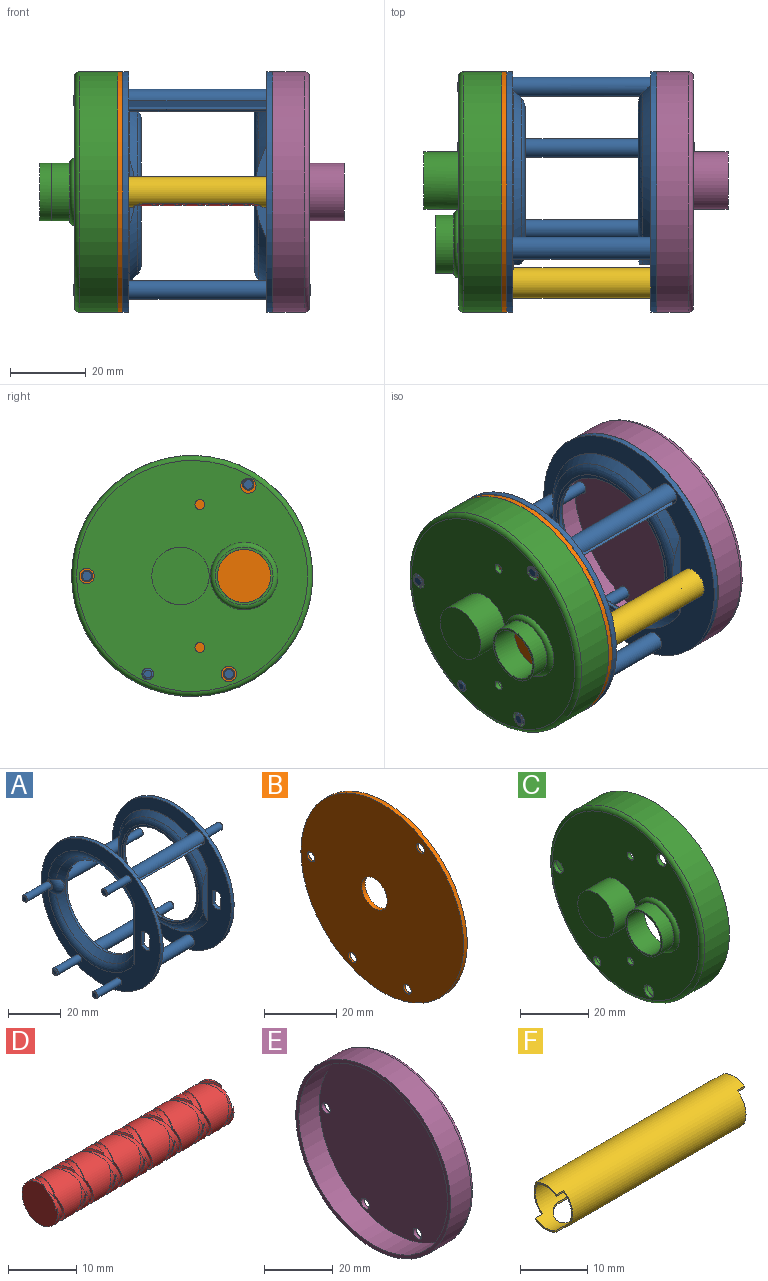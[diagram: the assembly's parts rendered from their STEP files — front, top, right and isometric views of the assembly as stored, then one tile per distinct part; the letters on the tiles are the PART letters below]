
ASSEMBLY  parts=6 mates=7
PART A: 81 faces, bbox 63.4x66.5x64.5 mm
  f0: plane 63.75x63.75mm, normal (1,0,0), area 1164.5mm2, adj f40,f46,f48,f49,f50,f51,f52,f60
  f1: cylinder r=25.35mm len=47.47mm, axis (1,0,0), area 6.6mm2, adj f4,f7,f43,f57
  f2: cylinder r=25.35mm len=28.84mm, axis (1,0,0), area 3.4mm2, adj f3,f7,f44,f57
  f3: cone r=22.17mm half-angle=45deg, axis (1,0,0), area 185.6mm2, adj f2,f6,f9,f43,f44,f57
  f4: cone r=22.17mm half-angle=45deg, axis (1,0,0), area 187.1mm2, adj f1,f6,f43,f57
  f5: cone r=23.94mm half-angle=45deg, axis (-1,0,0), area 390.7mm2, adj f10,f28,f43,f58
  f6: torus R=20.6mm, axis (-1,0,0), area 401.6mm2, adj f3,f4,f41,f43,f57
  f7: plane 63.75x63.75mm, normal (-1,0,0), area 1118.4mm2, adj f1,f2,f9,f38,f39,f40,f43,f44
  f8: plane 63.75x63.75mm, normal (1,0,0), area 1277.6mm2, adj f10,f14,f38,f39,f43,f44,f53,f54
  f9: cylinder r=25.35mm len=21.09mm, axis (1,0,0), area 2.8mm2, adj f3,f7,f43,f44
  f10: cylinder r=23.94mm len=47.88mm, axis (-1,0,0), area 14.8mm2, adj f5,f8,f43,f59
  f11: cone r=19.7mm half-angle=45deg, axis (-1,0,0), area 199.7mm2, adj f27,f30,f33,f35,f36
  f12: torus R=25.35mm, axis (1,0,0), area 204.3mm2, adj f13,f19,f29,f32,f35,f36,f37
  f13: plane 63.75x63.75mm, normal (-1,0,0), area 1200.4mm2, adj f12,f14,f15,f17,f19,f21,f30,f37
  f14: cylinder r=31.88mm len=63.75mm, axis (-1,0,0), area 310.3mm2, adj f8,f13
  f15: cylinder r=1.5mm len=12.8mm, axis (1,0,0), area 121.1mm2, adj f13,f24
  f16: plane 2.5x2.5mm, normal (-1,0,0), area 4.9mm2, adj f24
  f17: cylinder r=1.55mm len=12.55mm, axis (1,0,0), area 122.2mm2, adj f13,f23
  f18: plane 2.08x2.08mm, normal (-1,0,0), area 3.4mm2, adj f23
  f19: cylinder r=1.5mm len=12.83mm, axis (1,0,0), area 121.1mm2, adj f12,f13,f26,f30,f31,f32,f34
  f20: plane 2.5x2.5mm, normal (-1,0,0), area 4.9mm2, adj f26
  f21: cylinder r=1.5mm len=12.8mm, axis (1,0,0), area 121.1mm2, adj f13,f25
  f22: plane 2.5x2.5mm, normal (-1,0,0), area 4.9mm2, adj f25
  f23: torus R=1.04mm, axis (-1,0,0), area 6.8mm2, adj f17,f18
  f24: cone r=1.25mm half-angle=45deg, axis (1,0,0), area 3.1mm2, adj f15,f16
  f25: cone r=1.25mm half-angle=45deg, axis (1,0,0), area 3.1mm2, adj f21,f22
  f26: cone r=1.25mm half-angle=45deg, axis (1,0,0), area 3.1mm2, adj f19,f20
  f27: cylinder r=19.7mm len=39.4mm, axis (-1,0,0), area 125.7mm2, adj f11,f28,f29
  f28: torus R=19.15mm, axis (1,0,0), area 319.2mm2, adj f5,f27
  f29: cone r=19.7mm half-angle=45deg, axis (-1,0,0), area 199.7mm2, adj f12,f27,f33,f35,f36
  f30: torus R=25.35mm, axis (1,0,0), area 204.3mm2, adj f11,f13,f19,f31,f35,f36,f37
  f31: plane 0.8x0.04mm, normal (0,1,0), area 0mm2, adj f19,f30,f34,f35
  f32: plane 0.8x0.04mm, normal (0,1,0), area 0mm2, adj f12,f19,f34,f35
  f33: cylinder r=5.09mm len=4.45mm, axis (-1,0,0), area 1.5mm2, adj f11,f29,f35
  f34: plane 3.84x1.92mm, normal (-1,0,0), area 2.2mm2, adj f19,f31,f32,f35
  f35: torus R=1.92mm, axis (-1,0,0), area 35.6mm2, adj f11,f12,f29,f30,f31,f32,f33,f34
  f36: plane 20.64x2.55mm, normal (0,1,0), area 34.5mm2, adj f11,f12,f29,f30,f37
  f37: cylinder r=1.27mm len=28.49mm, axis (0,0,1), area 49mm2, adj f12,f13,f30,f36
  f38: cylinder r=2.93mm len=36.47mm, axis (-1,0,0), area 574.6mm2, adj f7,f8,f76,f77,f78,f79
  f39: cylinder r=2.49mm len=36.47mm, axis (-1,0,0), area 570.5mm2, adj f7,f8
  f40: cylinder r=31.88mm len=63.75mm, axis (-1,0,0), area 310.3mm2, adj f0,f7
  f41: plane 41.19x41.19mm, normal (-1,0,0), area 113.7mm2, adj f6,f42
  f42: cylinder r=19.7mm len=39.4mm, axis (-1,0,0), area 125.7mm2, adj f41,f45
  f43: cylinder r=2.49mm len=36.47mm, axis (-1,0,0), area 547.1mm2, adj f1,f3,f4,f5,f6,f7,f8,f9
  f44: cylinder r=2.49mm len=36.47mm, axis (-1,0,0), area 569mm2, adj f2,f3,f7,f8,f9
  f45: cone r=23.51mm half-angle=45deg, axis (1,0,0), area 449.8mm2, adj f42,f46,f47
  f46: torus R=25.35mm, axis (1,0,0), area 447.5mm2, adj f0,f45,f47,f48,f62
  f47: plane 14.82x1.28mm, normal (0,1,0), area 12.5mm2, adj f45,f46,f48
  f48: cylinder r=1.27mm len=24.34mm, axis (0,0,1), area 39.1mm2, adj f0,f46,f47
  f49: plane 6.81x1.55mm, normal (0,-1,0), area 10.5mm2, adj f0,f7,f50,f52
  f50: cylinder r=4.06mm len=4.45mm, axis (-1,0,0), area 7.3mm2, adj f0,f7,f49,f51
  f51: plane 6.81x1.55mm, normal (0,1,0), area 10.5mm2, adj f0,f7,f50,f52
  f52: cylinder r=4.06mm len=4.45mm, axis (-1,0,0), area 7.3mm2, adj f0,f7,f49,f51
  f53: plane 6.81x1.55mm, normal (0,-1,0), area 10.5mm2, adj f8,f13,f54,f56
  f54: cylinder r=4.06mm len=4.45mm, axis (-1,0,0), area 7.3mm2, adj f8,f13,f53,f55
  f55: plane 6.81x1.55mm, normal (0,1,0), area 10.5mm2, adj f8,f13,f54,f56
  f56: cylinder r=4.06mm len=4.45mm, axis (-1,0,0), area 7.3mm2, adj f8,f13,f53,f55
  f57: plane 25.06x3.62mm, normal (0,-1,0), area 49.9mm2, adj f1,f2,f3,f4,f6,f7
  f58: plane 17.74x1.71mm, normal (0,-1,0), area 20mm2, adj f5,f59
  f59: plane 17.73x1.7mm, normal (1,0,0), area 20.3mm2, adj f10,f58
  f60: cylinder r=1.59mm len=9.45mm, axis (-1,0,0), area 94.2mm2, adj f0,f61
  f61: plane 3.18x3.18mm, normal (1,0,0), area 4.6mm2, adj f60,f75
  f62: plane 3.18x2.15mm, normal (-1,0,0), area 5.7mm2, adj f46,f63
  f63: cylinder r=1.59mm len=9.45mm, axis (-1,0,0), area 94.2mm2, adj f0,f62,f64
  f64: plane 3.18x3.18mm, normal (1,0,0), area 4.6mm2, adj f63,f71
  f65: cylinder r=1.59mm len=9.58mm, axis (-1,0,0), area 95.5mm2, adj f0,f69
  f66: cylinder r=1.59mm len=9.45mm, axis (-1,0,0), area 94.2mm2, adj f0,f67
  f67: plane 3.18x3.18mm, normal (1,0,0), area 4.6mm2, adj f66,f73
  f68: plane 2.24x2.24mm, normal (1,0,0), area 3.9mm2, adj f69
  f69: torus R=1.12mm, axis (1,0,0), area 6.6mm2, adj f65,f68
  f70: cone r=1.03mm half-angle=59deg, axis (1,0,0), area 3.9mm2, adj f71
  f71: cylinder r=1.03mm len=6.1mm, axis (1,0,0), area 39.3mm2, adj f64,f70
  f72: cone r=1.03mm half-angle=59deg, axis (1,0,0), area 3.9mm2, adj f73
  f73: cylinder r=1.03mm len=6.1mm, axis (1,0,0), area 39.3mm2, adj f67,f72
  f74: cone r=1.03mm half-angle=59deg, axis (1,0,0), area 3.9mm2, adj f75
  f75: cylinder r=1.03mm len=6.1mm, axis (1,0,0), area 39.3mm2, adj f61,f74
  f76: plane 3.01x2.71mm, normal (1,0,0), area 5mm2, adj f38,f77,f79,f80
  f77: plane 36.4x1.51mm, normal (0,-0.38,0.92), area 59.3mm2, adj f38,f76,f78,f80
  f78: plane 3.01x2.71mm, normal (-1,0,0), area 5mm2, adj f38,f77,f79,f80
  f79: plane 36.4x1.72mm, normal (0,0.38,-0.92), area 67.7mm2, adj f38,f76,f78,f80
  f80: plane 36.4x2.39mm, normal (0,-0.92,-0.38), area 94mm2, adj f76,f77,f78,f79
PART B: 26 faces, bbox 5.8x63.6x63.6 mm
  f0: cylinder r=1.5mm len=3.01mm, axis (1,0,0), area 6.5mm2, adj f7,f20
  f1: cylinder r=1.55mm len=3.1mm, axis (1,0,0), area 6.7mm2, adj f7,f18
  f2: cylinder r=1.5mm len=3.01mm, axis (1,0,0), area 6.5mm2, adj f7,f16
  f3: cylinder r=1.5mm len=3.01mm, axis (1,0,0), area 6.5mm2, adj f7,f14
  f4: plane 41.1x41.1mm, normal (1,0,0), area 724.5mm2, adj f9,f10
  f5: plane 63.56x63.56mm, normal (1,0,0), area 1744.1mm2, adj f6,f9,f15,f17,f19,f21
  f6: cylinder r=31.78mm len=63.56mm, axis (-1,0,0), area 268.8mm2, adj f5,f7
  f7: plane 63.56x63.56mm, normal (-1,0,0), area 3064.7mm2, adj f0,f1,f2,f3,f6,f8
  f8: cylinder r=5.04mm len=10.07mm, axis (-1,0,0), area 42.6mm2, adj f7,f12
  f9: cylinder r=20.55mm len=41.1mm, axis (-1,0,0), area 154.1mm2, adj f4,f5
  f10: cylinder r=13.84mm len=27.69mm, axis (-1,0,0), area 287.2mm2, adj f4,f11
  f11: plane 27.69x27.69mm, normal (1,0,0), area 64.5mm2, adj f10,f13
  f12: plane 26.16x26.16mm, normal (1,0,0), area 457.9mm2, adj f8,f13
  f13: cylinder r=13.08mm len=26.16mm, axis (1,0,0), area 369.5mm2, adj f11,f12
  f14: plane 4.45x4.45mm, normal (1,0,0), area 8.4mm2, adj f3,f22
  f15: cylinder r=2.86mm len=5.72mm, axis (1,0,0), area 0.5mm2, adj f5,f22
  f16: plane 4.45x4.45mm, normal (1,0,0), area 8.4mm2, adj f2,f25
  f17: cylinder r=2.86mm len=5.72mm, axis (1,0,0), area 0.5mm2, adj f5,f25
  f18: plane 4.45x4.45mm, normal (1,0,0), area 8mm2, adj f1,f24
  f19: cylinder r=2.86mm len=5.72mm, axis (1,0,0), area 0.5mm2, adj f5,f24
  f20: plane 4.45x4.45mm, normal (1,0,0), area 8.4mm2, adj f0,f23
  f21: cylinder r=2.86mm len=5.72mm, axis (1,0,0), area 0.5mm2, adj f5,f23
  f22: cone r=2.22mm half-angle=45deg, axis (1,0,0), area 14.3mm2, adj f14,f15
  f23: cone r=2.22mm half-angle=45deg, axis (1,0,0), area 14.3mm2, adj f20,f21
  f24: cone r=2.22mm half-angle=45deg, axis (1,0,0), area 14.3mm2, adj f18,f19
  f25: cone r=2.22mm half-angle=45deg, axis (1,0,0), area 14.3mm2, adj f16,f17
PART C: 20 faces, bbox 20.6x68.9x68.9 mm
  f0: plane 61.09x61.09mm, normal (-1,0,0), area 2442.8mm2, adj f5,f6,f10,f11,f12,f13,f14,f16
  f1: cylinder r=31.81mm len=63.63mm, axis (-1,0,0), area 2030.9mm2, adj f2,f5
  f2: plane 63.63x63.63mm, normal (1,0,0), area 248.8mm2, adj f1,f3
  f3: cylinder r=30.54mm len=61.09mm, axis (1,0,0), area 1949.8mm2, adj f2,f4
  f4: plane 61.09x61.09mm, normal (1,0,0), area 2710.9mm2, adj f3,f9,f10,f11,f12,f13,f16,f17
  f5: torus R=30.54mm, axis (1,0,0), area 393mm2, adj f0,f1
  f6: torus R=7.66mm, axis (-1,0,0), area 106.1mm2, adj f0,f7
  f7: cylinder r=7.66mm len=15.32mm, axis (1,0,0), area 229.8mm2, adj f6,f8
  f8: plane 15.32x15.32mm, normal (-1,0,0), area 29.3mm2, adj f7,f9
  f9: cylinder r=7.02mm len=14.05mm, axis (-1,0,0), area 322.8mm2, adj f4,f8
  f10: cylinder r=2.03mm len=4.06mm, axis (-1,0,0), area 16.2mm2, adj f0,f4
  f11: cylinder r=2.03mm len=4.06mm, axis (-1,0,0), area 16.2mm2, adj f0,f4
  f12: cylinder r=1.3mm len=2.59mm, axis (-1,0,0), area 10.3mm2, adj f0,f4
  f13: cylinder r=1.3mm len=2.59mm, axis (-1,0,0), area 10.3mm2, adj f0,f4
  f14: cylinder r=7.58mm len=15.16mm, axis (1,0,0), area 436.8mm2, adj f0,f15
  f15: plane 15.16x15.16mm, normal (-1,0,0), area 180.6mm2, adj f14
  f16: cylinder r=2.03mm len=4.06mm, axis (-1,0,0), area 16.2mm2, adj f0,f4
  f17: cylinder r=1.55mm len=3.1mm, axis (-1,0,0), area 12.4mm2, adj f0,f4
  f18: cylinder r=1.59mm len=8.26mm, axis (1,0,0), area 82.3mm2, adj f4,f19
  f19: plane 3.18x3.18mm, normal (1,0,0), area 7.9mm2, adj f18
PART D: 76 faces, bbox 39.2x8.2x8.3 mm
  f0: cylinder r=3.68mm len=7.37mm, axis (-1,0,0), area 48.8mm2, adj f33,f37,f42,f43
  f1: cylinder r=3.68mm len=7.37mm, axis (-1,0,0), area 48.8mm2, adj f22,f32,f45,f46
  f2: cylinder r=3.68mm len=7.37mm, axis (-1,0,0), area 48.8mm2, adj f21,f31,f48,f49
  f3: cylinder r=3.68mm len=7.37mm, axis (-1,0,0), area 48.8mm2, adj f20,f30,f51,f52
  f4: cylinder r=3.68mm len=7.37mm, axis (-1,0,0), area 48.8mm2, adj f19,f29,f54,f55
  f5: cylinder r=3.68mm len=7.37mm, axis (-1,0,0), area 48.8mm2, adj f18,f28,f57,f58
  f6: cylinder r=3.68mm len=7.37mm, axis (-1,0,0), area 48.8mm2, adj f17,f27,f60,f61
  f7: cylinder r=3.68mm len=7.37mm, axis (-1,0,0), area 48.8mm2, adj f16,f26,f63,f64
  f8: cylinder r=3.68mm len=7.37mm, axis (-1,0,0), area 48.8mm2, adj f15,f25,f66,f67
  f9: cylinder r=3.68mm len=7.37mm, axis (-1,0,0), area 48.8mm2, adj f14,f24,f69,f70
  f10: cylinder r=3.68mm len=7.37mm, axis (-1,0,0), area 48.8mm2, adj f13,f23,f72,f75
  f11: cylinder r=3.68mm len=7.37mm, axis (-1,0,0), area 24.4mm2, adj f12,f35,f73
  f12: bspline ~7.27x5.52mm, area 3.4mm2, adj f11,f35,f39,f73
  f13: bspline ~7.27x5.52mm, area 3.4mm2, adj f10,f39,f72,f75
  f14: bspline ~7.27x5.52mm, area 3.4mm2, adj f9,f39,f69,f70
  f15: bspline ~7.27x5.52mm, area 3.4mm2, adj f8,f39,f66,f67
  f16: bspline ~7.27x5.52mm, area 3.4mm2, adj f7,f39,f63,f64
  f17: bspline ~7.27x5.52mm, area 3.4mm2, adj f6,f39,f60,f61
  f18: bspline ~7.27x5.52mm, area 3.4mm2, adj f5,f39,f57,f58
  f19: bspline ~7.27x5.52mm, area 3.4mm2, adj f4,f39,f54,f55
  f20: bspline ~7.27x5.52mm, area 3.4mm2, adj f3,f39,f51,f52
  f21: bspline ~7.27x5.52mm, area 3.4mm2, adj f2,f39,f48,f49
  f22: bspline ~7.27x5.52mm, area 3.4mm2, adj f1,f39,f45,f46
  f23: bspline ~7.78x5.84mm, area 3.4mm2, adj f10,f39,f72,f75
  f24: bspline ~7.78x5.84mm, area 3.4mm2, adj f9,f39,f69,f70
  f25: bspline ~7.78x5.84mm, area 3.4mm2, adj f8,f39,f66,f67
  f26: bspline ~7.78x5.84mm, area 3.4mm2, adj f7,f39,f63,f64
  f27: bspline ~7.78x5.84mm, area 3.4mm2, adj f6,f39,f60,f61
  f28: bspline ~7.78x5.84mm, area 3.4mm2, adj f5,f39,f57,f58
  f29: bspline ~7.78x5.84mm, area 3.4mm2, adj f4,f39,f54,f55
  f30: bspline ~7.78x5.84mm, area 3.4mm2, adj f3,f39,f51,f52
  f31: bspline ~7.78x5.84mm, area 3.4mm2, adj f2,f39,f48,f49
  f32: bspline ~7.78x5.84mm, area 3.4mm2, adj f1,f39,f45,f46
  f33: bspline ~7.78x5.84mm, area 3.4mm2, adj f0,f39,f42,f43
  f34: cylinder r=3.68mm len=7.37mm, axis (-1,0,0), area 24.4mm2, adj f36,f38,f40
  f35: plane 7.38x7.38mm, normal (1,0,0), area 41.4mm2, adj f11,f12,f39,f73
  f36: plane 7.38x7.38mm, normal (-1,0,0), area 41.4mm2, adj f34,f38,f39,f40
  f37: bspline ~8.1x5.52mm, area 3.4mm2, adj f0,f39,f42,f43
  f38: bspline ~7.78x5.84mm, area 3.4mm2, adj f34,f36,f39,f40
  f39: bspline ~39.23x6.86mm, area 128.1mm2, adj f12,f13,f14,f15,f16,f17,f18,f19
  f40: bspline ~8.1x5.52mm, area 3.4mm2, adj f34,f36,f38,f41
  f41: bspline ~6.37x6.03mm, area 8.9mm2, adj f39,f40,f42
  f42: bspline ~6.68x5.84mm, area 3.4mm2, adj f0,f33,f37,f41
  f43: bspline ~8.1x5.52mm, area 3.4mm2, adj f0,f33,f37,f44
  f44: bspline ~6.37x6.03mm, area 8.9mm2, adj f39,f43,f45
  f45: bspline ~7.78x5.84mm, area 3.4mm2, adj f1,f22,f32,f44
  f46: bspline ~8.1x5.52mm, area 3.4mm2, adj f1,f22,f32,f47
  f47: bspline ~6.37x6.03mm, area 8.9mm2, adj f39,f46,f48
  f48: bspline ~7.78x5.84mm, area 3.4mm2, adj f2,f21,f31,f47
  f49: bspline ~8.1x5.52mm, area 3.4mm2, adj f2,f21,f31,f50
  f50: bspline ~6.37x6.03mm, area 8.9mm2, adj f39,f49,f51
  f51: bspline ~7.78x5.84mm, area 3.4mm2, adj f3,f20,f30,f50
  f52: bspline ~8.1x5.52mm, area 3.4mm2, adj f3,f20,f30,f53
  f53: bspline ~6.37x6.03mm, area 8.9mm2, adj f39,f52,f54
  f54: bspline ~7.78x5.84mm, area 3.4mm2, adj f4,f19,f29,f53
  f55: bspline ~8.1x5.52mm, area 3.4mm2, adj f4,f19,f29,f56
  f56: bspline ~6.37x6.03mm, area 8.9mm2, adj f39,f55,f57
  f57: bspline ~7.78x5.84mm, area 3.4mm2, adj f5,f18,f28,f56
  f58: bspline ~8.1x5.52mm, area 3.4mm2, adj f5,f18,f28,f59
  f59: bspline ~6.37x6.03mm, area 8.9mm2, adj f39,f58,f60
  f60: bspline ~7.78x5.84mm, area 3.4mm2, adj f6,f17,f27,f59
  f61: bspline ~8.1x5.52mm, area 3.4mm2, adj f6,f17,f27,f62
  f62: bspline ~6.37x6.03mm, area 8.9mm2, adj f39,f61,f63
  f63: bspline ~7.78x5.84mm, area 3.4mm2, adj f7,f16,f26,f62
  f64: bspline ~8.1x5.52mm, area 3.4mm2, adj f7,f16,f26,f65
  f65: bspline ~6.37x6.03mm, area 8.9mm2, adj f39,f64,f66
  f66: bspline ~7.78x5.84mm, area 3.4mm2, adj f8,f15,f25,f65
  f67: bspline ~8.1x5.52mm, area 3.4mm2, adj f8,f15,f25,f68
  f68: bspline ~6.37x6.03mm, area 8.9mm2, adj f39,f67,f69
  f69: bspline ~7.78x5.84mm, area 3.4mm2, adj f9,f14,f24,f68
  f70: bspline ~8.1x5.52mm, area 3.4mm2, adj f9,f14,f24,f71
  f71: bspline ~6.37x6.03mm, area 8.9mm2, adj f39,f70,f72
  f72: bspline ~7.78x5.84mm, area 3.4mm2, adj f10,f13,f23,f71
  f73: bspline ~7.78x5.84mm, area 3.4mm2, adj f11,f12,f35,f74
  f74: bspline ~6.03x5.44mm, area 8.9mm2, adj f39,f73,f75
  f75: bspline ~7.27x5.52mm, area 3.4mm2, adj f10,f13,f23,f74
PART E: 12 faces, bbox 18.9x68.9x68.9 mm
  f0: plane 61.09x61.09mm, normal (1,0,0), area 2711.3mm2, adj f5,f6,f7,f8,f9,f10
  f1: cylinder r=31.81mm len=63.63mm, axis (-1,0,0), area 1690.7mm2, adj f2,f5
  f2: plane 63.63x63.63mm, normal (-1,0,0), area 248.8mm2, adj f1,f3
  f3: cylinder r=30.54mm len=61.09mm, axis (-1,0,0), area 1623.2mm2, adj f2,f4
  f4: plane 61.09x61.09mm, normal (-1,0,0), area 2891.9mm2, adj f3,f6,f7,f8,f9
  f5: torus R=30.54mm, axis (1,0,0), area 393mm2, adj f0,f1
  f6: cylinder r=1.76mm len=3.52mm, axis (1,0,0), area 14mm2, adj f0,f4
  f7: cylinder r=1.76mm len=3.52mm, axis (1,0,0), area 14mm2, adj f0,f4
  f8: cylinder r=1.76mm len=3.52mm, axis (1,0,0), area 14mm2, adj f0,f4
  f9: cylinder r=1.76mm len=3.52mm, axis (1,0,0), area 14mm2, adj f0,f4
  f10: cylinder r=7.58mm len=15.16mm, axis (-1,0,0), area 436.8mm2, adj f0,f11
  f11: plane 15.16x15.16mm, normal (1,0,0), area 180.6mm2, adj f10
PART F: 22 faces, bbox 39.6x8.1x8.1 mm
  f0: plane 1.55x0.31mm, normal (0,-1,0), area 0.5mm2, adj f2,f9,f10,f17
  f1: plane 1.55x0.31mm, normal (0,1,0), area 0.5mm2, adj f8,f9,f13,f17
  f2: plane 4.45x0.97mm, normal (1,0,0), area 1.2mm2, adj f0,f9,f12,f17
  f3: plane 1.55x0.31mm, normal (0,1,0), area 0.5mm2, adj f7,f9,f16,f17
  f4: plane 1.55x0.31mm, normal (0,-1,0), area 0.5mm2, adj f5,f6,f9,f17
  f5: plane 4.45x0.97mm, normal (-1,0,0), area 1.2mm2, adj f4,f9,f14,f17
  f6: plane 6.81x1.84mm, normal (-1,0,0), area 1.9mm2, adj f4,f9,f15,f17
  f7: plane 6.81x1.84mm, normal (-1,0,0), area 1.9mm2, adj f3,f9,f14,f17
  f8: plane 6.81x1.84mm, normal (1,0,0), area 1.9mm2, adj f1,f9,f12,f17
  f9: cylinder r=4.06mm len=39.57mm, axis (-1,0,0), area 777.7mm2, adj f0,f1,f2,f3,f4,f5,f6,f7
  f10: plane 6.81x1.84mm, normal (1,0,0), area 1.9mm2, adj f0,f9,f11,f17
  f11: plane 1.55x0.31mm, normal (0,-1,0), area 0.5mm2, adj f9,f10,f13,f17
  f12: plane 1.55x0.31mm, normal (0,1,0), area 0.5mm2, adj f2,f8,f9,f17
  f13: plane 4.45x0.97mm, normal (1,0,0), area 1.2mm2, adj f1,f9,f11,f17
  f14: plane 1.55x0.31mm, normal (0,1,0), area 0.5mm2, adj f5,f7,f9,f17
  f15: plane 1.55x0.31mm, normal (0,-1,0), area 0.5mm2, adj f6,f9,f16,f17
  f16: plane 4.45x0.97mm, normal (-1,0,0), area 1.2mm2, adj f3,f9,f15,f17
  f17: cylinder r=3.81mm len=39.57mm, axis (1,0,0), area 717.4mm2, adj f0,f1,f2,f3,f4,f5,f6,f7
  f18: cylinder r=2.54mm len=5.08mm, axis (0,0,1), area 2.3mm2, adj f9,f17,f19,f21
  f19: plane 29.41x0.33mm, normal (0,-1,0), area 9.8mm2, adj f9,f17,f18,f20
  f20: cylinder r=2.54mm len=5.08mm, axis (0,0,1), area 2.3mm2, adj f9,f17,f19,f21
  f21: plane 29.41x0.33mm, normal (0,1,0), area 9.8mm2, adj f9,f17,f18,f20
PLACE A t=(-19.91,-0.24,1.05)mm fixed
PLACE B t=(-21.25,-0.24,1.05)mm
PLACE C t=(-32.68,-0.24,1.05)mm
PLACE D rot(axis=(-1,0,0),8.4deg) t=(-19.91,-24.3,1.05)mm
PLACE E t=(19.67,-0.24,1.05)mm
PLACE F t=(-18.36,-24.3,1.05)mm
MATE cylindrical B.f2 <-> A.f19  axis (-1,0,0) through (-21.25,27.63,1.05)mm
MATE fastened F.f9 <-> A.f50  axis (1,0,0) through (18.12,-24.3,1.05)mm
MATE fastened C.f1 <-> B.f6  axis (1,0,0) through (-21.25,-0.24,1.05)mm
MATE cylindrical C.f17 <-> A.f17  axis (-1,0,0) through (-32.68,11.47,-24.86)mm
MATE revolute D.f0 <-> F.f9  axis (-1,0,0) through (-19.91,-24.3,1.05)mm
MATE fastened E.f1 <-> A.f14  axis (-1,0,0) through (19.67,-0.24,1.05)mm
MATE fastened B.f1 <-> A.f17  axis (1,0,0) through (-19.91,11.47,-24.86)mm
